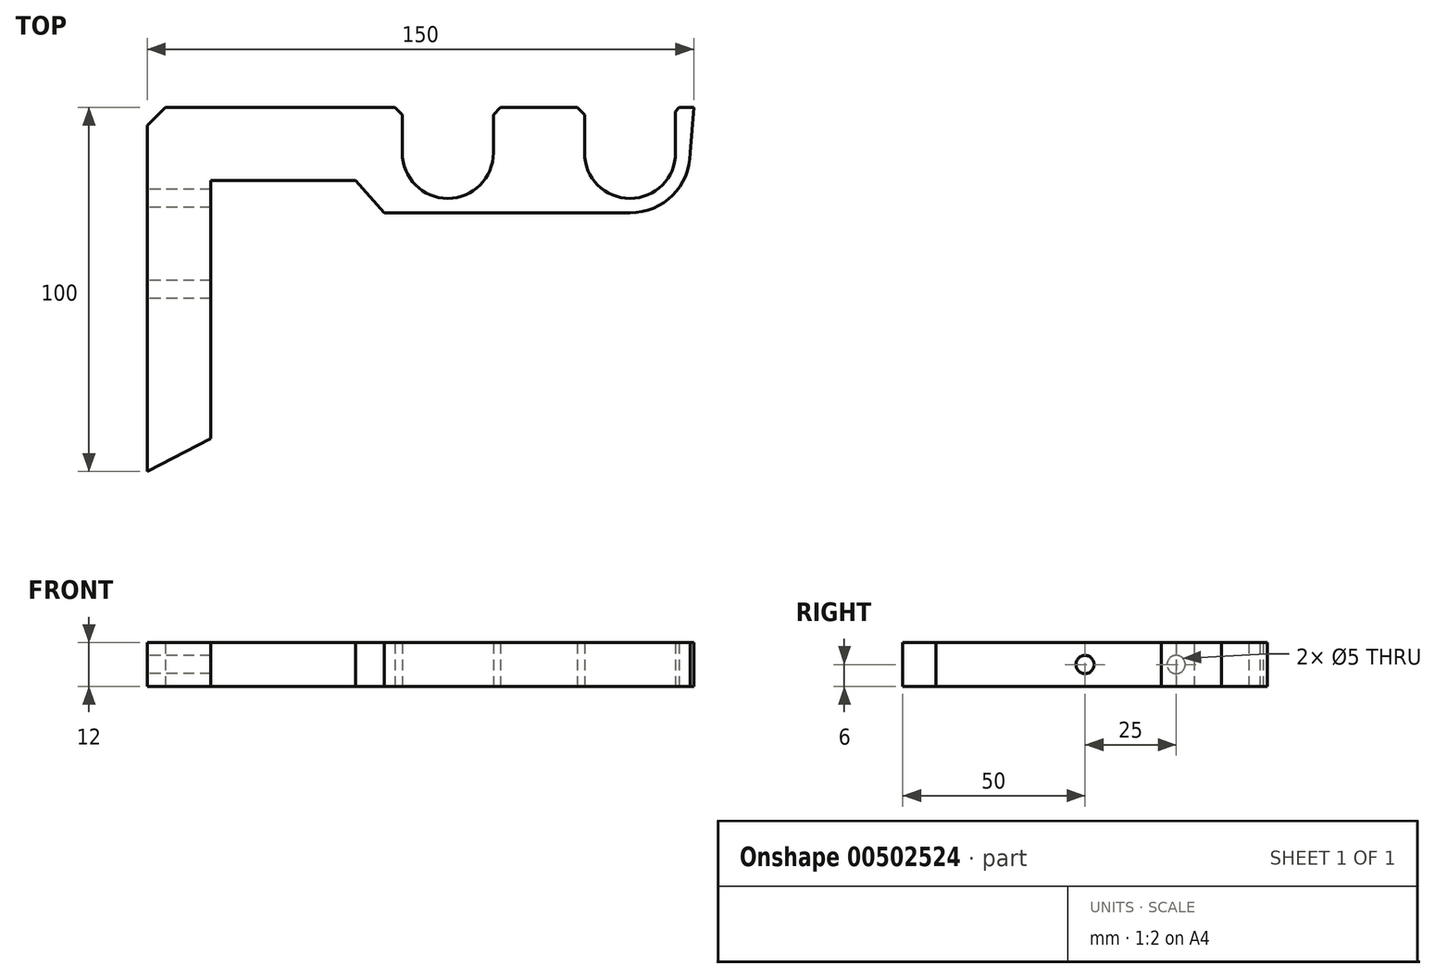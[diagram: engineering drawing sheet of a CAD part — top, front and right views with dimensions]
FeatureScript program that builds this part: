
annotation { "Feature Type Name" : "Feature", "Feature Type Description" : "" }
export const myFeature = defineFeature(function(context is Context, id is Id, definition is map)
    precondition{}
    {
        {
            var Q0;
            Q0=qCreatedBy(makeId("Top.planeOp"),FACE);
            var sketch = newSketch(context, id + "F0", { "sketchPlane" : qUnion([Q0])});
            skLineSegment(sketch, "E0.top", {"start": v(70, -25) * mm, "end": v(95, -25) * mm, "construction": true});
            skLineSegment(sketch, "E1.top", {"start": v(120, -25) * mm, "end": v(145, -25) * mm, "construction": true});
            skLineSegment(sketch, "E1.left", {"start": v(120, 0) * mm, "end": v(120, -25) * mm, "construction": true});
            skPoint(sketch, "E2.centerSnap0", {"position": v(70, -12.5) * mm});
            skPoint(sketch, "E2.centerSnap1", {"position": v(82.5, -25) * mm});
            skPoint(sketch, "E3.centerSnap0", {"position": v(120, -12.5) * mm});
            skPoint(sketch, "E3.centerSnap1", {"position": v(132.5, -25) * mm});
            skPoint(sketch, "E4", {"position": v(5, 0) * mm});
            skPoint(sketch, "E5", {"position": v(0, -5) * mm});
            skLineSegment(sketch, "E6", {"start": v(0, -5) * mm, "end": v(5, 0) * mm});
            skArc(sketch, "E7", {"start": v(70, -12.5) * mm, "mid": v(82.5, -25) * mm, "end": v(95, -12.5) * mm});
            skArc(sketch, "E8", {"start": v(120, -12.5) * mm, "mid": v(132.5, -25) * mm, "end": v(145, -12.5) * mm});
            skLineSegment(sketch, "E9", {"start": v(120, 0) * mm, "end": v(120, -12.5) * mm});
            skLineSegment(sketch, "E10", {"start": v(145, -3.33) * mm, "end": v(145, -12.5) * mm});
            skArc(sketch, "E11.0", {"start": v(116, -12.5) * mm, "mid": v(132.5, -29) * mm, "end": v(149, -12.5) * mm});
            skLineSegment(sketch, "E12", {"start": v(150, 0) * mm, "end": v(149, -12.5) * mm});
            skPoint(sketch, "E13", {"position": v(68, 0) * mm});
            skPoint(sketch, "E14", {"position": v(70, -2) * mm});
            skPoint(sketch, "E15", {"position": v(95, -2) * mm});
            skLineSegment(sketch, "E16", {"start": v(5, 0) * mm, "end": v(68, 0) * mm});
            skLineSegment(sketch, "E17", {"start": v(68, 0) * mm, "end": v(70, -2) * mm});
            skLineSegment(sketch, "E18", {"start": v(70, -2) * mm, "end": v(70, -12.5) * mm});
            skLineSegment(sketch, "E19", {"start": v(95, -12.5) * mm, "end": v(95, -2) * mm});
            skPoint(sketch, "E20", {"position": v(120, -2) * mm});
            skPoint(sketch, "E21", {"position": v(145.97, 0) * mm});
            skPoint(sketch, "E22", {"position": v(145, -1.16) * mm});
            skLineSegment(sketch, "E23", {"start": v(145, -1.16) * mm, "end": v(145, -3.33) * mm});
            skLineSegment(sketch, "E24", {"start": v(145, -1.16) * mm, "end": v(145.97, 0) * mm});
            skLineSegment(sketch, "E25", {"start": v(145.97, 0) * mm, "end": v(150, 0) * mm});
            skLineSegment(sketch, "E26", {"start": v(27.49, -85.7) * mm, "end": v(0, -100) * mm});
            skLineSegment(sketch, "E27", {"start": v(132.5, -29) * mm, "end": v(108.43, -38.18) * mm});
            skLineSegment(sketch, "E28", {"start": v(27.49, -85.7) * mm, "end": v(108.43, -38.18) * mm});
            skLineSegment(sketch, "E29", {"start": v(0, -5) * mm, "end": v(0, -30) * mm});
            skLineSegment(sketch, "E30", {"start": v(0, -35) * mm, "end": v(0, -60) * mm});
            skLineSegment(sketch, "E31", {"start": v(0, -65) * mm, "end": v(0, -100) * mm});
            skLineSegment(sketch, "E32", {"start": v(150, 0) * mm, "end": v(0, 0) * mm, "construction": true});
            skPoint(sketch, "E33", {"position": v(97, 0) * mm});
            skPoint(sketch, "E34", {"position": v(118, 0) * mm});
            skLineSegment(sketch, "E35", {"start": v(95, -2) * mm, "end": v(97, 0) * mm});
            skLineSegment(sketch, "E36", {"start": v(118, 0) * mm, "end": v(120, -2) * mm});
            skLineSegment(sketch, "E37", {"start": v(97, 0) * mm, "end": v(118, 0) * mm});
            skLineSegment(sketch, "E38.bottom", {"start": v(132.5, -29) * mm, "end": v(17.49, -29) * mm});
            skLineSegment(sketch, "E38.top", {"start": v(132.5, -90.9) * mm, "end": v(17.49, -90.9) * mm});
            skLineSegment(sketch, "E38.left", {"start": v(132.5, -29) * mm, "end": v(132.5, -90.9) * mm});
            skLineSegment(sketch, "E38.right", {"start": v(17.49, -29) * mm, "end": v(17.49, -90.9) * mm});
            skLineSegment(sketch, "E39", {"start": v(0, -30) * mm, "end": v(0, -35) * mm});
            skLineSegment(sketch, "E40", {"start": v(0, -60) * mm, "end": v(0, -65) * mm});
            skLineSegment(sketch, "E41.bottom", {"start": v(17.49, -46.2) * mm, "end": v(57.2, -46.2) * mm});
            skLineSegment(sketch, "E41.top", {"start": v(17.49, -20.11) * mm, "end": v(57.2, -20.11) * mm});
            skLineSegment(sketch, "E41.left", {"start": v(17.49, -46.2) * mm, "end": v(17.49, -20.11) * mm});
            skLineSegment(sketch, "E41.right", {"start": v(57.2, -46.2) * mm, "end": v(57.2, -20.11) * mm});
            skLineSegment(sketch, "E42", {"start": v(57.2, -20.11) * mm, "end": v(65.11, -29) * mm});
            skSolve(sketch);
        }
        {
            var Q0;
            Q0=makeQuery(id+"F0.imprint","IMPRINT",FACE,{"disambiguationData":[TD([[makeQuery(id+"F0.imprint","IMPRINT",EDGE,{"derivedFrom":sQuery(id+"F0.wireOp",EDGE,"E6")}),-1.0]])]});
            var Q1;
            {var subQ0=sQuery(id+"F0.wireOp",EDGE,"Qdvw1bdW-gEd1-lqR0-xPgH-J3jiwdF8YBYC");Q1=makeQuery(id+"F0.imprint","IMPRINT",FACE,{"disambiguationData":[TD([[makeQuery(id+"F0.imprint","IMPRINT",EDGE,{"derivedFrom":subQ0}),1.0]])]});}
            var Q2;
            {var subQ0=sQuery(id+"F0.wireOp",EDGE,"m36aCPex-EKpa-QvQQ-mRmz-YUSPYPZwudMs");Q2=makeQuery(id+"F0.imprint","IMPRINT",FACE,{"disambiguationData":[TD([[makeQuery(id+"F0.imprint","IMPRINT",EDGE,{"derivedFrom":subQ0}),1.0]])]});}
            extrude(context, id + "F1", {"entities" : qUnion([Q0, Q1, Q2]), "depth" : 12 * mm});
        }
        {
            var Q0;
            {var subQ2=sQuery(id+"F0.wireOp",EDGE,"E27");Q0=makeQuery(id+"F0.imprint","IMPRINT",FACE,{"disambiguationData":[TD([[makeQuery(id+"F0.imprint","IMPRINT",EDGE,{"derivedFrom":subQ2}),-1.0]])]});}
            extrude(context, id + "F2", {"entities" : qUnion([Q0]), "operationType" : NewBodyOperationType.REMOVE, "oppositeDirection" : true, "depth" : 25 * mm});
        }
        {
            var Q0;
            Q0=makeQuery(id+"F1.opExtrude","SWEPT_FACE",FACE,{"disambiguationData":[OSD([sQuery(id+"F0.wireOp",EDGE,"E29"),sQuery(id+"F0.wireOp",EDGE,"E30"),sQuery(id+"F0.wireOp",EDGE,"E31"),sQuery(id+"F0.wireOp",EDGE,"E39"),sQuery(id+"F0.wireOp",EDGE,"E40")])]});
            var sketch = newSketch(context, id + "F3", { "sketchPlane" : qUnion([Q0])});
            skLineSegment(sketch, "E43", {"start": v(100, 6) * mm, "end": v(0, 6) * mm, "construction": true});
            skCircle(sketch, "E44", {"center": v(25, 6) * mm, "radius": 2.5 * mm});
            skCircle(sketch, "E45", {"center": v(50, 6) * mm, "radius": 2.5 * mm});
            skSolve(sketch);
        }
        {
            var Q0;
            Q0=makeQuery(id+"F3.imprint","IMPRINT",FACE,{"disambiguationData":[TD([[makeQuery(id+"F3.imprint","IMPRINT",EDGE,{"derivedFrom":sQuery(id+"F3.wireOp",EDGE,"E44")}),1.0]])]});
            var Q1;
            Q1=makeQuery(id+"F3.imprint","IMPRINT",FACE,{"disambiguationData":[TD([[makeQuery(id+"F3.imprint","IMPRINT",EDGE,{"derivedFrom":sQuery(id+"F3.wireOp",EDGE,"E45")}),1.0]])]});
            extrude(context, id + "F4", {"entities" : qUnion([Q0, Q1]), "operationType" : NewBodyOperationType.REMOVE, "oppositeDirection" : true, "depth" : 25 * mm});
        }
    });
